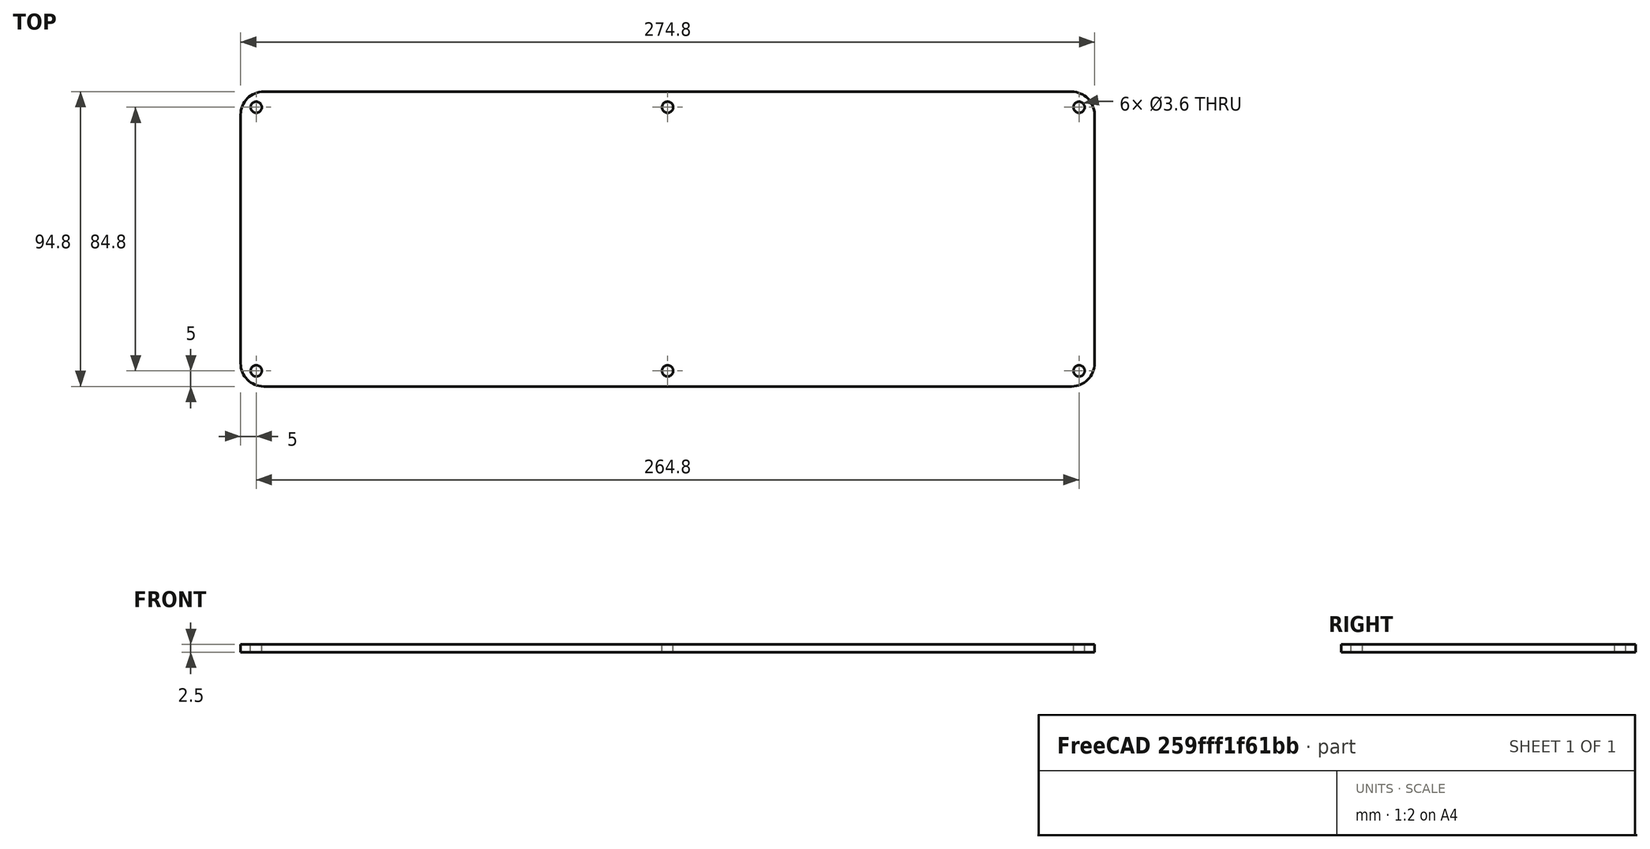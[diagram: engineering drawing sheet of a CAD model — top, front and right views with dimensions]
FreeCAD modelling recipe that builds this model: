
FCSTD DOCUMENT  (FreeCAD 1.0R39285 (Git))
Label: TopEnclosureBack
License: All rights reserved
LicenseURL: https://en.wikipedia.org/wiki/All_rights_reserved
objects: PartDesign::SubShapeBinder×3, PartDesign::Mirrored×3, App::Link×2, PartDesign::Hole×2, PartDesign::Pad×1, PartDesign::MultiTransform×1, PartDesign::Body×1
note: 21 computed .brp shape members not serialized (recipe doc carries the construction recipe); baked Part::Feature solids carry a one-line shape summary decoded from their .brp
EXTERNAL_REF file=Spec.FCStd obj=Spreadsheet
EXTERNAL_REF file=TopEnclosure.FCStd obj=Sketch

FEATURE [App::Link] Link  label="Vars"
  LinkedObject = -> <external Spec.FCStd>#Spreadsheet
FEATURE [App::Link] Link001  label="MasterSketch"
  LinkedObject = -> <external TopEnclosure.FCStd>#Sketch
FEATURE [PartDesign::SubShapeBinder] Binder
  BindCopyOnChange = 0
  BindMode = 0
  ClaimChildren = false
  Context = -> Body [Binder.]
  Fuse = false
  MakeFace = true
  OffsetFill = false
  OffsetIntersection = false
  OffsetJoinType = 0
  OffsetOpenResult = false
  PartialLoad = false
  Refine = true
  Relative = true
  Support = -> [Link001[Edge9,Edge16,Edge15,Edge14,Edge13,Edge12,Edge11,Edge10]]
  _Version = 2
FEATURE [PartDesign::SubShapeBinder] Binder001
  BindCopyOnChange = 0
  BindMode = 0
  ClaimChildren = false
  Context = -> Body [Binder001.]
  Fuse = false
  MakeFace = true
  OffsetFill = false
  OffsetIntersection = false
  OffsetJoinType = 0
  OffsetOpenResult = false
  PartialLoad = false
  Refine = true
  Relative = true
  Support = -> [Link001[Edge39]]
  _Version = 2
FEATURE [PartDesign::SubShapeBinder] Binder002
  BindCopyOnChange = 0
  BindMode = 0
  ClaimChildren = false
  Context = -> Body [Binder002.]
  Fuse = false
  MakeFace = true
  OffsetFill = false
  OffsetIntersection = false
  OffsetJoinType = 0
  OffsetOpenResult = false
  PartialLoad = false
  Refine = true
  Relative = true
  Support = -> [Link001[Edge40]]
  _Version = 2
FEATURE [PartDesign::Pad] Pad
  Direction = (0,0,1)
  Length = 2.5
  Length2 = 10
  Profile = -> Binder
  Refine = true
  Suppressed = false
  Type = 0
  expr: Length = <<Vars>>.wall
FEATURE [PartDesign::Hole] Hole
  BaseFeature = -> Pad
  CustomThreadClearance = 0
  Depth = 25
  DepthType = 0
  Diameter = 3.6
  DrillForDepth = false
  DrillPoint = 1
  DrillPointAngle = 118
  HoleCutCountersinkAngle = 90
  HoleCutCustomValues = false
  HoleCutDepth = 0
  HoleCutDiameter = 6.1
  HoleCutType = 0
  ModelThread = false
  Profile = -> Binder001
  Refine = true
  Reversed = true
  Suppressed = false
  Tapered = false
  TaperedAngle = 90
  ThreadClass = 0
  ThreadDepth = 25
  ThreadDepthType = 0
  ThreadDirection = 0
  ThreadFit = 2
  ThreadSize = 9
  ThreadType = 1
  Threaded = false
  UseCustomThreadClearance = false
FEATURE [PartDesign::Mirrored] Mirrored
  MirrorPlane = -> YZ_Plane
  Refine = true
  Suppressed = false
  TransformMode = 0
FEATURE [PartDesign::Mirrored] Mirrored001
  MirrorPlane = -> XZ_Plane
  Refine = true
  Suppressed = false
  TransformMode = 0
FEATURE [PartDesign::MultiTransform] MultiTransform
  BaseFeature = -> Hole
  Originals = -> [Hole]
  Refine = true
  Suppressed = false
  TransformMode = 0
  Transformations = -> [Mirrored,Mirrored001]
FEATURE [PartDesign::Hole] Hole001
  BaseFeature = -> MultiTransform
  CustomThreadClearance = 0
  Depth = 25
  DepthType = 0
  Diameter = 3.6
  DrillForDepth = false
  DrillPoint = 1
  DrillPointAngle = 118
  HoleCutCountersinkAngle = 90
  HoleCutCustomValues = false
  HoleCutDepth = 0
  HoleCutDiameter = 6.1
  HoleCutType = 0
  ModelThread = false
  Profile = -> Binder002
  Refine = true
  Reversed = true
  Suppressed = false
  Tapered = false
  TaperedAngle = 90
  ThreadClass = 0
  ThreadDepth = 25
  ThreadDepthType = 0
  ThreadDirection = 0
  ThreadFit = 2
  ThreadSize = 9
  ThreadType = 1
  Threaded = false
  UseCustomThreadClearance = false
FEATURE [PartDesign::Mirrored] Mirrored002
  BaseFeature = -> Hole001
  MirrorPlane = -> XZ_Plane
  Originals = -> [Hole001]
  Refine = true
  Suppressed = false
  TransformMode = 0
FEATURE [PartDesign::Body] Body  label="Top Enclosure Back"
  AllowCompound = false
  Group = -> [Binder,Binder001,Binder002,Pad,Hole,MultiTransform,Mirrored,Mirrored001,Hole001,Mirrored002]
  Origin = -> Origin
  Tip = -> Mirrored002

RESOLVED EXTERNAL PARTS (link-assembly join: the EXTERNAL_REF files above that resolve inside this repo's crawl, each included once):
---- part Spec.FCStd = doc fcstd_a8ec68f4a39c ----
FCSTD DOCUMENT  (FreeCAD 1.0R39319 (Git))
Label: Spec
License: All rights reserved
LicenseURL: https://en.wikipedia.org/wiki/All_rights_reserved
objects: Spreadsheet::Sheet×1

FEATURE [Spreadsheet::Sheet] Spreadsheet  label="Vars"
  cells = A1='Common; A2='clearance; B2(clearance)=0.2; A3='nut_inserts_m2; B3(nut_inserts_m2)=3.5; A4='nut_inserts_m3; B4(nut_inserts_m3)=4.5; A5='wall; B5(wall)=2.5; A6='ext_radius; B6(ext_radius)=10; A7='hood_angle; B7(hood_angle)=4; A12='Display; A13='display_width; B13(display_width)=231.3; A14='display_height; B14(display_height)=64.3; A15='display_depth; B15(display_depth)=5.5; A16='display_offset_bottom; B16(display_offset_bottom)==3 + display_view_offset; C16='display_view_offset; D16(display_view_offset)=1; A17='display_offset_left; B17(display_offset_left)==2.5 + display_view_offset; A18='display_offset_right; B18(display_offset_right)==7.5 + display_view_offset; A19='display_offset_top; B19(display_offset_top)==3 + display_view_offset; F20='b; A21='Top Enclosure; A22='top_enclosure_width; B22(top_enclosure_width)=280; A23='top_enclosure_height; B23(top_enclosure_height)=100; A24='top_enclosure_front_depth; B24(top_enclosure_front_depth)=1; A25='top_enclosure_back_depth; B25(top_enclosure_back_depth)==wall; A26='top_enclosure_display_back_depth; B26(top_enclosure_display_back_depth)=1; A27='top_enclosure_depth; B27(top_enclosure_depth)=14; A28='top_enclosure_internal_depth; B28(top_enclosure_internal_depth)==top_enclosure_depth - top_enclosure_front_depth - display_depth - top_enclosure_display_back_depth - top_enclosure_back_depth + wall; A30='Bottom Enclosure; A31='bottom_enclosure_width; B31(bottom_enclosure_width)==top_enclosure_width; A32='bottom_enclosure_height; B32(bottom_enclosure_height)=160; A33='bottom_enclosure_depth; B33(bottom_enclosure_depth)=30; A35='Keyboard Plate; A36='keyboard_plate_width; B36(keyboard_plate_width)==235 - 2; A37='keyboard_plate_height; B37(keyboard_plate_height)==82.5 - 2; A38='keyboard_plate_radius; B38(kayboard_plate_radius)==ext_radius / 2; A40='Keyboard Plate; A41='wire_hole_offset_x; B41(wire_hole_offset_x)=40; A42='wire_hole_width; B42(wire_hole_width)=30; A43='wire_hole_height; B43(wire_hole_height)=9
---- part TopEnclosure.FCStd = doc fcstd_a96d0c470227 ----
FCSTD DOCUMENT  (FreeCAD 1.0R39319 (Git))
Label: TopEnclosure
License: All rights reserved
LicenseURL: https://en.wikipedia.org/wiki/All_rights_reserved
objects: App::Link×1, Sketcher::SketchObject×1
note: 2 computed .brp shape members not serialized (recipe doc carries the construction recipe); baked Part::Feature solids carry a one-line shape summary decoded from their .brp
EXTERNAL_REF file=Spec.FCStd obj=Spreadsheet

FEATURE [App::Link] Link  label="Vars"
  LinkedObject = -> <external Spec.FCStd>#Spreadsheet
FEATURE [Sketcher::SketchObject] Sketch  label="MasterSketch"
  ArcFitTolerance = 1e-06
  FullyConstrained = true
  MakeInternals = false
  expr: Constraints[100] = <<Vars>>.display_offset_left
  expr: Constraints[101] = <<Vars>>.display_offset_right
  expr: Constraints[102] = <<Vars>>.display_offset_bottom
  expr: Constraints[150] = <<Vars>>.ext_radius
  expr: Constraints[64] = <<Vars>>.wall
  expr: Constraints[65] = <<Vars>>.top_enclosure_height
  expr: Constraints[66] = <<Vars>>.top_enclosure_width
  expr: Constraints[67] = <<Vars>>.clearance / 2
  expr: Constraints[96] = <<Vars>>.display_width + <<Vars>>.clearance
  expr: Constraints[97] = <<Vars>>.display_height + <<Vars>>.clearance
  expr: Constraints[99] = <<Vars>>.display_offset_top
  sketch-geometry (62):
    g0: LineSegment StartX=-137.5 StartY=40 StartZ=0 EndX=-137.5 EndY=-40 EndZ=0
    g1: LineSegment StartX=-130 StartY=-47.5 StartZ=0 EndX=130 EndY=-47.5 EndZ=0
    g2: LineSegment StartX=137.5 StartY=-40 StartZ=0 EndX=137.5 EndY=40 EndZ=0
    g3: LineSegment StartX=130 StartY=47.5 StartZ=0 EndX=-130 EndY=47.5 EndZ=0
    g4: ArcOfCircle CenterX=-130 CenterY=40 CenterZ=0 NormalX=0 NormalY=0 NormalZ=1 AngleXU=0 Radius=7.5 StartAngle=1.5708 EndAngle=3.14159
    g5: ArcOfCircle CenterX=-130 CenterY=-40 CenterZ=0 NormalX=0 NormalY=0 NormalZ=1 AngleXU=0 Radius=7.5 StartAngle=3.14159 EndAngle=4.71239
    g6: ArcOfCircle CenterX=130 CenterY=-40 CenterZ=0 NormalX=0 NormalY=0 NormalZ=1 AngleXU=0 Radius=7.5 StartAngle=4.71239 EndAngle=6.28319
    g7: ArcOfCircle CenterX=130 CenterY=40 CenterZ=0 NormalX=0 NormalY=0 NormalZ=1 AngleXU=0 Radius=7.5 StartAngle=4e-16 EndAngle=1.5708
    g8: GeomPoint [constr] X=-137.5 Y=47.5 Z=0
    g9: GeomPoint [constr] X=137.5 Y=-47.5 Z=0
    g10: LineSegment StartX=-137.4 StartY=40 StartZ=0 EndX=-137.4 EndY=-40 EndZ=0
    g11: LineSegment StartX=-130 StartY=-47.4 StartZ=0 EndX=130 EndY=-47.4 EndZ=0
    g12: LineSegment StartX=137.4 StartY=-40 StartZ=0 EndX=137.4 EndY=40 EndZ=0
    g13: LineSegment StartX=130 StartY=47.4 StartZ=0 EndX=-130 EndY=47.4 EndZ=0
    g14: ArcOfCircle CenterX=-130 CenterY=40 CenterZ=0 NormalX=0 NormalY=0 NormalZ=1 AngleXU=0 Radius=7.4 StartAngle=1.5708 EndAngle=3.14159
    g15: ArcOfCircle CenterX=-130 CenterY=-40 CenterZ=0 NormalX=0 NormalY=0 NormalZ=1 AngleXU=0 Radius=7.4 StartAngle=3.14159 EndAngle=4.71239
    g16: ArcOfCircle CenterX=130 CenterY=-40 CenterZ=0 NormalX=0 NormalY=0 NormalZ=1 AngleXU=0 Radius=7.4 StartAngle=4.71239 EndAngle=6.28319
    g17: ArcOfCircle CenterX=130 CenterY=40 CenterZ=0 NormalX=0 NormalY=0 NormalZ=1 AngleXU=0 Radius=7.4 StartAngle=3e-16 EndAngle=1.5708
    g18: GeomPoint [constr] X=-137.4 Y=47.4 Z=0
    g19: GeomPoint [constr] X=137.4 Y=-47.4 Z=0
    g20: LineSegment StartX=-140 StartY=40 StartZ=0 EndX=-140 EndY=-40 EndZ=0
    g21: LineSegment StartX=-130 StartY=-50 StartZ=0 EndX=130 EndY=-50 EndZ=0
    g22: LineSegment StartX=140 StartY=-40 StartZ=0 EndX=140 EndY=40 EndZ=0
    g23: LineSegment StartX=130 StartY=50 StartZ=0 EndX=-130 EndY=50 EndZ=0
    g24: ArcOfCircle CenterX=-130 CenterY=40 CenterZ=0 NormalX=0 NormalY=0 NormalZ=1 AngleXU=0 Radius=10 StartAngle=1.5708 EndAngle=3.14159
    g25: ArcOfCircle CenterX=-130 CenterY=-40 CenterZ=0 NormalX=0 NormalY=0 NormalZ=1 AngleXU=0 Radius=10 StartAngle=3.14159 EndAngle=4.71239
    g26: ArcOfCircle CenterX=130 CenterY=-40 CenterZ=0 NormalX=0 NormalY=0 NormalZ=1 AngleXU=0 Radius=10 StartAngle=4.71239 EndAngle=6.28319
    g27: ArcOfCircle CenterX=130 CenterY=40 CenterZ=0 NormalX=0 NormalY=0 NormalZ=1 AngleXU=0 Radius=10 StartAngle=0 EndAngle=1.5708
    g28: GeomPoint [constr] X=-140 Y=50 Z=0
    g29: GeomPoint [constr] X=140 Y=-50 Z=0
    g30: LineSegment StartX=-109.75 StartY=24.25 StartZ=0 EndX=-109.75 EndY=-24.25 EndZ=0
    g31: LineSegment StartX=-105.75 StartY=-28.25 StartZ=0 EndX=105.75 EndY=-28.25 EndZ=0
    g32: LineSegment StartX=109.75 StartY=-24.25 StartZ=0 EndX=109.75 EndY=24.25 EndZ=0
    g33: LineSegment StartX=105.75 StartY=28.25 StartZ=0 EndX=-105.75 EndY=28.25 EndZ=0
    g34: ArcOfCircle CenterX=-105.75 CenterY=24.25 CenterZ=0 NormalX=0 NormalY=0 NormalZ=1 AngleXU=0 Radius=4 StartAngle=1.5708 EndAngle=3.14159
    g35: ArcOfCircle CenterX=-105.75 CenterY=-24.25 CenterZ=0 NormalX=0 NormalY=0 NormalZ=1 AngleXU=0 Radius=4 StartAngle=3.14159 EndAngle=4.71239
    g36: ArcOfCircle CenterX=105.75 CenterY=-24.25 CenterZ=0 NormalX=0 NormalY=0 NormalZ=1 AngleXU=0 Radius=4 StartAngle=4.71239 EndAngle=6.28319
    g37: ArcOfCircle CenterX=105.75 CenterY=24.25 CenterZ=0 NormalX=0 NormalY=0 NormalZ=1 AngleXU=0 Radius=4 StartAngle=0 EndAngle=1.5708
    g38: GeomPoint [constr] X=-109.75 Y=28.25 Z=0
    g39: GeomPoint [constr] X=109.75 Y=-28.25 Z=0
    g40: LineSegment StartX=-113.25 StartY=32.25 StartZ=0 EndX=-113.25 EndY=-32.25 EndZ=0
    g41: LineSegment StartX=-113.25 StartY=-32.25 StartZ=0 EndX=118.25 EndY=-32.25 EndZ=0
    g42: LineSegment StartX=118.25 StartY=-32.25 StartZ=0 EndX=118.25 EndY=32.25 EndZ=0
    g43: LineSegment StartX=118.25 StartY=32.25 StartZ=0 EndX=-113.25 EndY=32.25 EndZ=0
    g44: Circle CenterX=-137.703 CenterY=47.7033 CenterZ=0 NormalX=0 NormalY=0 NormalZ=1 AngleXU=0 Radius=12.5
    g45: Circle CenterX=0 CenterY=49.9 CenterZ=0 NormalX=0 NormalY=0 NormalZ=1 AngleXU=0 Radius=12.5
    g46: Circle CenterX=-132.4 CenterY=42.4 CenterZ=0 NormalX=0 NormalY=0 NormalZ=1 AngleXU=0 Radius=1.5
    g47: Circle CenterX=0 CenterY=42.4 CenterZ=0 NormalX=0 NormalY=0 NormalZ=1 AngleXU=0 Radius=1.5
    g48: LineSegment [constr] StartX=0 StartY=42.4 StartZ=0 EndX=0 EndY=37.4 EndZ=0
    g49: LineSegment [constr] StartX=-132.4 StartY=42.4 StartZ=0 EndX=-128.864 EndY=38.8645 EndZ=0
    g50: LineSegment [constr] StartX=-132.4 StartY=42.4 StartZ=0 EndX=-137.703 EndY=47.7033 EndZ=0
    g51: LineSegment StartX=121.25 StartY=26.25 StartZ=0 EndX=121.25 EndY=25.25 EndZ=0
    g52: LineSegment StartX=122.25 StartY=24.25 StartZ=0 EndX=130.25 EndY=24.25 EndZ=0
    g53: LineSegment StartX=131.25 StartY=25.25 StartZ=0 EndX=131.25 EndY=26.25 EndZ=0
    g54: LineSegment StartX=130.25 StartY=27.25 StartZ=0 EndX=122.25 EndY=27.25 EndZ=0
    g55: ArcOfCircle CenterX=122.25 CenterY=26.25 CenterZ=0 NormalX=0 NormalY=0 NormalZ=1 AngleXU=0 Radius=1 StartAngle=1.5708 EndAngle=3.14159
    g56: ArcOfCircle CenterX=122.25 CenterY=25.25 CenterZ=0 NormalX=0 NormalY=0 NormalZ=1 AngleXU=0 Radius=1 StartAngle=3.14159 EndAngle=4.71239
    g57: ArcOfCircle CenterX=130.25 CenterY=25.25 CenterZ=0 NormalX=0 NormalY=0 NormalZ=1 AngleXU=0 Radius=1 StartAngle=4.71239 EndAngle=6.28319
    g58: ArcOfCircle CenterX=130.25 CenterY=26.25 CenterZ=0 NormalX=0 NormalY=0 NormalZ=1 AngleXU=0 Radius=1 StartAngle=1e-16 EndAngle=1.5708
    g59: GeomPoint [constr] X=121.25 Y=27.25 Z=0
    g60: GeomPoint [constr] X=131.25 Y=24.25 Z=0
    g61: LineSegment [constr] StartX=126.25 StartY=32.25 StartZ=0 EndX=126.25 EndY=-32.25 EndZ=0
  constraints (151):
    c: Tangent(g0,g4) = -1.5708
    c: Tangent(g0,g5) = -1.5708
    c: Tangent(g1,g5) = -1.5708
    c: Tangent(g1,g6) = -1.5708
    c: Tangent(g2,g6) = -1.5708
    c: Tangent(g2,g7) = -1.5708
    c: Tangent(g3,g7) = -1.5708
    c: Tangent(g3,g4) = -1.5708
    c: Vertical(g0)
    c: Vertical(g2)
    c: Horizontal(g1)
    c: Horizontal(g3)
    c: Equal(g4,g5)
    c: Equal(g5,g6)
    c: Equal(g6,g7)
    c: PointOnObject(g8,g0)
    c: PointOnObject(g8,g3)
    c: PointOnObject(g9,g1)
    c: PointOnObject(g9,g2)
    c: Tangent(g10,g14) = -1.5708
    c: Tangent(g10,g15) = -1.5708
    c: Tangent(g11,g15) = -1.5708
    c: Tangent(g11,g16) = -1.5708
    c: Tangent(g12,g16) = -1.5708
    c: Tangent(g12,g17) = -1.5708
    c: Tangent(g13,g17) = -1.5708
    c: Tangent(g13,g14) = -1.5708
    c: Vertical(g10)
    c: Vertical(g12)
    c: Horizontal(g11)
    c: Horizontal(g13)
    c: Equal(g14,g15)
    c: Equal(g15,g16)
    c: Equal(g16,g17)
    c: PointOnObject(g18,g10)
    c: PointOnObject(g18,g13)
    c: PointOnObject(g19,g11)
    c: PointOnObject(g19,g12)
    c: Tangent(g20,g24) = -1.5708
    c: Tangent(g20,g25) = -1.5708
    c: Tangent(g21,g25) = -1.5708
    c: Tangent(g21,g26) = -1.5708
    c: Tangent(g22,g26) = -1.5708
    c: Tangent(g22,g27) = -1.5708
    c: Tangent(g23,g27) = -1.5708
    c: Tangent(g23,g24) = -1.5708
    c: Vertical(g20)
    c: Vertical(g22)
    c: Horizontal(g21)
    c: Horizontal(g23)
    c: Equal(g24,g25)
    c: Equal(g25,g26)
    c: Equal(g26,g27)
    c: PointOnObject(g28,g20)
    c: PointOnObject(g28,g23)
    c: PointOnObject(g29,g21)
    c: PointOnObject(g29,g22)
    c: Symmetric(g25,g27,g-1)
    c: Symmetric(g5,g7,g-1)
    c: Symmetric(g15,g17,g-1)
    c: Horizontal(g20,g0)
    c: Horizontal(g0,g10)
    c: Vertical(g13,g3)
    c: Vertical(g3,g23)
    c: DistanceX(g20,g0) = 2.5
    c: DistanceY(g21,g23) = 100
    c: DistanceX(g20,g22) = 280
    c: DistanceY(g13,g3) = 0.1
    c: Tangent(g30,g34) = -1.5708
    c: Tangent(g30,g35) = -1.5708
    c: Tangent(g31,g35) = -1.5708
    c: Tangent(g31,g36) = -1.5708
    c: Tangent(g32,g36) = -1.5708
    c: Tangent(g32,g37) = -1.5708
    c: Tangent(g33,g37) = -1.5708
    c: Tangent(g33,g34) = -1.5708
    c: Vertical(g30)
    c: Vertical(g32)
    c: Horizontal(g31)
    c: Horizontal(g33)
    c: Equal(g34,g35)
    c: Equal(g35,g36)
    c: Equal(g36,g37)
    c: PointOnObject(g38,g30)
    c: PointOnObject(g38,g33)
    c: PointOnObject(g39,g31)
    c: PointOnObject(g39,g32)
    c: Coincident(g40,g41)
    c: Coincident(g41,g42)
    c: Coincident(g42,g43)
    c: Coincident(g43,g40)
    c: Vertical(g40)
    c: Vertical(g42)
    c: Horizontal(g41)
    c: Horizontal(g43)
    c: Symmetric(g35,g37,g-1)
    c: DistanceX(g41,g41) = 231.5
    c: DistanceY(g42,g42) = 64.5
    c: Radius(g34) = 4
    c: DistanceY(g33,g40) = 4
    c: DistanceX(g40,g30) = 3.5
    c: DistanceX(g32,g42) = 8.5
    c: DistanceY(g41,g31) = 4
    c: PointOnObject(g45,g-2)
    c: PointOnObject(g47,g-2)
    c: Equal(g46,g47)
    c: Equal(g45,g44)
    c: Diameter(g45) = 25
    c: Coincident(g48,g47)
    c: PointOnObject(g48,g45)
    c: Vertical(g48)
    c: DistanceY(g48,g48) = 5
    c: Horizontal(g47,g46)
    c: Coincident(g49,g46)
    c: PointOnObject(g49,g44)
    c: Equal(g49,g48)
    c: PointOnObject(g4,g49)
    c: Coincident(g50,g46)
    c: Coincident(g50,g44)
    c: Parallel(g49,g50)
    c: PointOnObject(g28,g50)
    c: DistanceY(g46,g13) = 5
    c: Diameter(g46) = 3
    c: Tangent(g51,g55) = -1.5708
    c: Tangent(g51,g56) = -1.5708
    c: Tangent(g52,g56) = -1.5708
    c: Tangent(g52,g57) = -1.5708
    c: Tangent(g53,g57) = -1.5708
    c: Tangent(g53,g58) = -1.5708
    c: Tangent(g54,g58) = -1.5708
    c: Tangent(g54,g55) = -1.5708
    c: Vertical(g51)
    c: Vertical(g53)
    c: Horizontal(g52)
    c: Horizontal(g54)
    c: Equal(g55,g56)
    c: Equal(g56,g57)
    c: Equal(g57,g58)
    c: PointOnObject(g59,g51)
    c: PointOnObject(g59,g54)
    c: PointOnObject(g60,g52)
    c: PointOnObject(g60,g53)
    c: Radius(g56) = 1
    c: DistanceY(g52,g54) = 3
    c: DistanceX(g51,g53) = 10
    c: Equal(g42,g61)
    c: Horizontal(g42,g61)
    c: DistanceX(g42,g61) = 8
    c: Symmetric(g54,g54,g61)
    c: DistanceY(g54,g42) = 5
    c: Radius(g25) = 10
